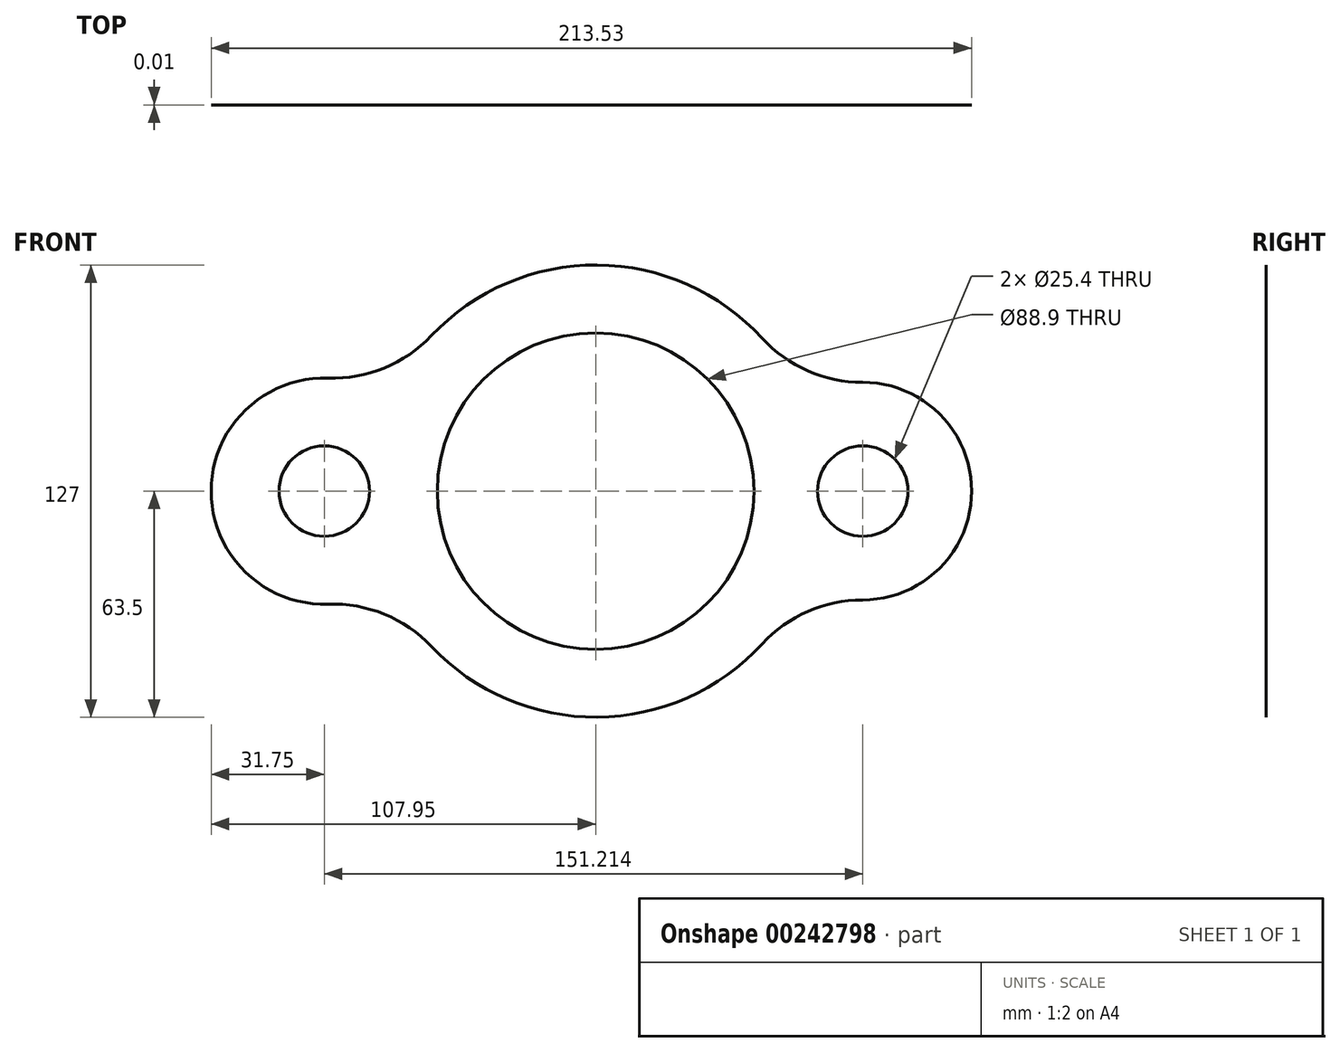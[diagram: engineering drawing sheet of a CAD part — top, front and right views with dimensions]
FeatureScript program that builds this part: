
annotation { "Feature Type Name" : "Feature", "Feature Type Description" : "" }
export const myFeature = defineFeature(function(context is Context, id is Id, definition is map)
    precondition{}
    {
        {
            var Q0;
            Q0=qCreatedBy(makeId("Front.planeOp"),FACE);
            var sketch = newSketch(context, id + "F0", { "sketchPlane" : qUnion([Q0])});
            skCircle(sketch, "E0", {"center": v(0, 0) * mm, "radius": 44.45 * mm});
            skCircle(sketch, "E1", {"center": v(75.01, 0) * mm, "radius": 12.7 * mm});
            skCircle(sketch, "E2", {"center": v(-76.2, 0) * mm, "radius": 12.7 * mm});
            skArc(sketch, "E3", {"start": v(74.96, -30.56) * mm, "mid": v(105.58, 0) * mm, "end": v(74.96, 30.56) * mm});
            skArc(sketch, "E4", {"start": v(-75.12, 31.73) * mm, "mid": v(-107.95, 0) * mm, "end": v(-75.12, -31.73) * mm});
            skArc(sketch, "E5", {"start": v(-46.14, -43.63) * mm, "mid": v(0.49, -63.5) * mm, "end": v(46.8, -42.92) * mm});
            skArc(sketch, "E6.trimOffspring", {"start": v(46.8, 42.92) * mm, "mid": v(0.49, 63.5) * mm, "end": v(-46.14, 43.63) * mm});
            skPoint(sketch, "E7.visualSharp", {"position": v(-57.94, 25.98) * mm});
            skArc(sketch, "E7.filletArc", {"start": v(-75.12, 31.73) * mm, "mid": v(-59.35, 34.56) * mm, "end": v(-46.14, 43.63) * mm});
            skPoint(sketch, "E8.visualSharp", {"position": v(58.16, 25.5) * mm});
            skArc(sketch, "E8.filletArc", {"start": v(46.8, 42.92) * mm, "mid": v(59.58, 33.77) * mm, "end": v(74.96, 30.56) * mm});
            skPoint(sketch, "E9.visualSharp", {"position": v(58.16, -25.5) * mm});
            skArc(sketch, "E9.filletArc", {"start": v(74.96, -30.56) * mm, "mid": v(59.58, -33.77) * mm, "end": v(46.8, -42.92) * mm});
            skPoint(sketch, "E10.visualSharp", {"position": v(-57.94, -25.98) * mm});
            skArc(sketch, "E10.filletArc", {"start": v(-46.14, -43.63) * mm, "mid": v(-59.35, -34.56) * mm, "end": v(-75.12, -31.73) * mm});
            skPoint(sketch, "E11.endSnap0", {"position": v(0.49, -63.5) * mm});
            skLineSegment(sketch, "E12", {"start": v(0, 0) * mm, "end": v(0.49, -63.5) * mm});
            skLineSegment(sketch, "E13", {"start": v(74.96, -30.56) * mm, "end": v(75.01, 0) * mm});
            skSolve(sketch);
        }
        {
            var Q0;
            Q0 = qSketchRegion(id + "F0", true);
            extrude(context, id + "F1", {"entities" : qUnion([Q0]), "depth" : 1 / 101.6 * mm});
        }
    });
